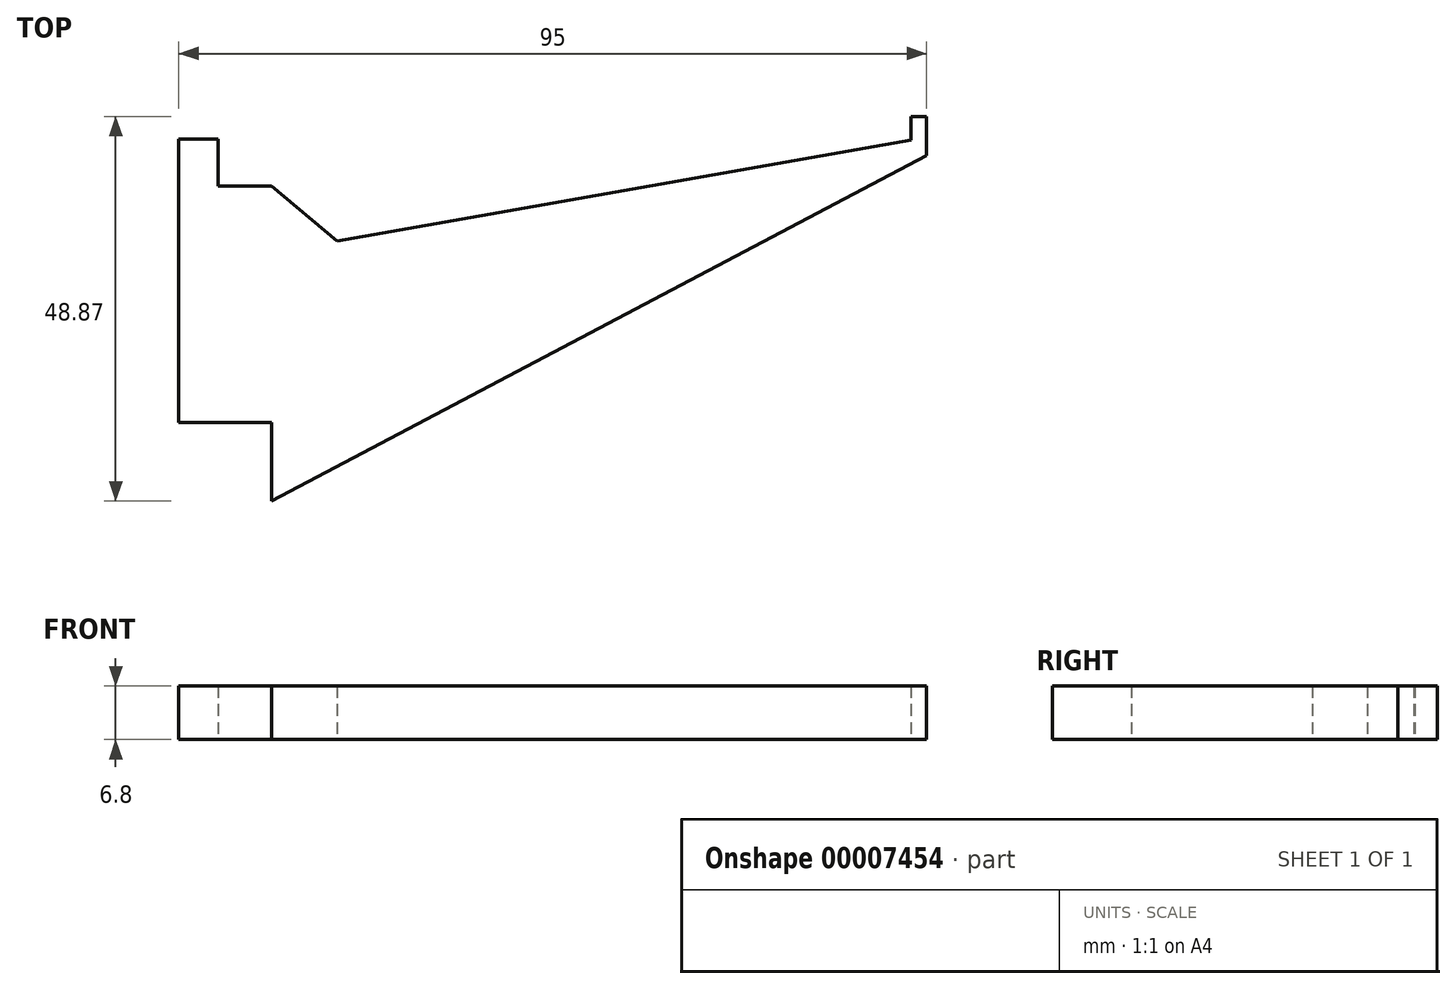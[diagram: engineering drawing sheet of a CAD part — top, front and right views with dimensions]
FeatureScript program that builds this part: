
annotation { "Feature Type Name" : "Feature", "Feature Type Description" : "" }
export const myFeature = defineFeature(function(context is Context, id is Id, definition is map)
    precondition{}
    {
        {
            var Q0;
            Q0=qCreatedBy(makeId("Top.planeOp"),FACE);
            var sketch = newSketch(context, id + "F0", { "sketchPlane" : qUnion([Q0])});
            skLineSegment(sketch, "E0", {"start": v(-6.8, 0) * mm, "end": v(0, 0) * mm});
            skLineSegment(sketch, "E1", {"start": v(-11.8, 36) * mm, "end": v(-11.8, 0) * mm});
            skLineSegment(sketch, "E2", {"start": v(0, 0) * mm, "end": v(0, 32) * mm, "construction": true});
            skLineSegment(sketch, "E3", {"start": v(0, 30) * mm, "end": v(-6.8, 30) * mm});
            skLineSegment(sketch, "E4", {"start": v(-6.8, 30) * mm, "end": v(-6.8, 36) * mm});
            skLineSegment(sketch, "E5", {"start": v(-6.8, 30) * mm, "end": v(-6.8, 0) * mm, "construction": true});
            skLineSegment(sketch, "E6", {"start": v(-11.8, 36) * mm, "end": v(-6.8, 36) * mm});
            skLineSegment(sketch, "E7", {"start": v(-6.8, 0) * mm, "end": v(-11.8, 0) * mm});
            skLineSegment(sketch, "E8", {"start": v(0, 0) * mm, "end": v(0, -10) * mm});
            skLineSegment(sketch, "E9", {"start": v(0, -10) * mm, "end": v(83.2, 33.87) * mm});
            skLineSegment(sketch, "E10", {"start": v(83.2, 33.87) * mm, "end": v(83.2, 38.87) * mm});
            skLineSegment(sketch, "E11", {"start": v(83.2, 38.87) * mm, "end": v(81.2, 38.87) * mm});
            skLineSegment(sketch, "E12", {"start": v(81.2, 38.87) * mm, "end": v(81.2, 35.87) * mm});
            skLineSegment(sketch, "E13", {"start": v(81.2, 35.87) * mm, "end": v(8.32, 23.02) * mm});
            skLineSegment(sketch, "E14", {"start": v(8.32, 23.02) * mm, "end": v(0, 30) * mm});
            skSolve(sketch);
        }
        {
            var Q0;
            Q0 = qSketchRegion(id + "F0", true);
            extrude(context, id + "F1", {"entities" : qUnion([Q0]), "depth" : 6.8 * mm});
        }
    });
